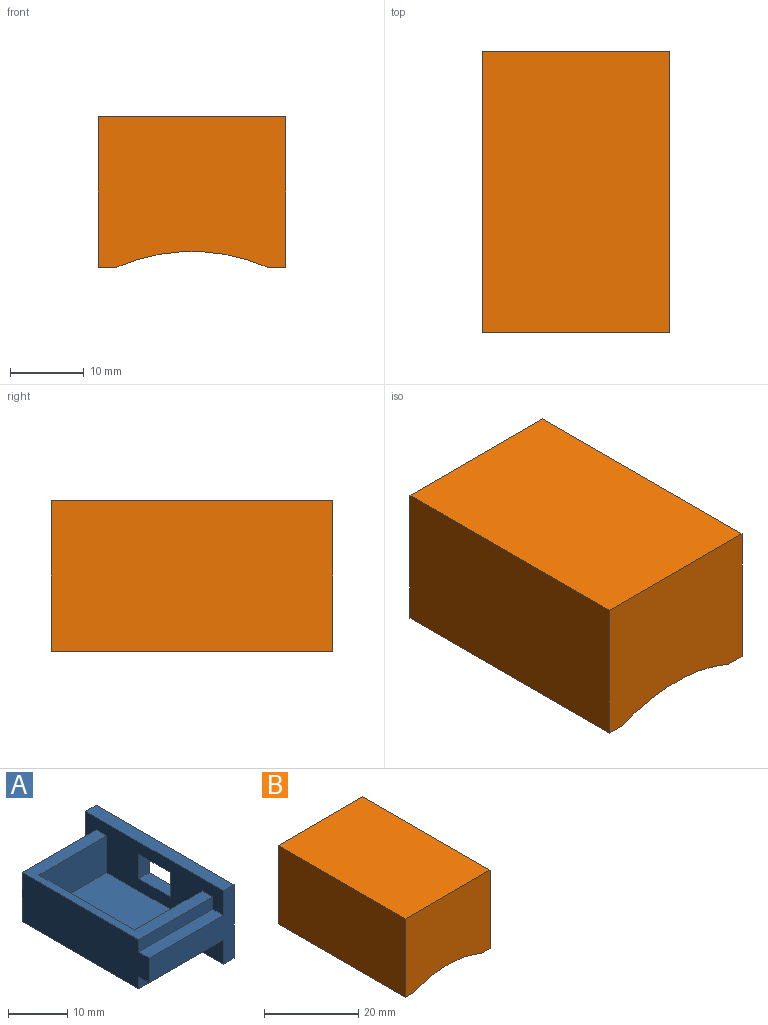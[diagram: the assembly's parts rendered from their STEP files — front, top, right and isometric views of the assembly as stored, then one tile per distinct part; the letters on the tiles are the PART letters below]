
ASSEMBLY  parts=2 mates=1
PART A: 22 faces, bbox 20.3x33x15.2 mm
  f0: plane 27.94x17.78mm, normal (0,0,1), area 125.2mm2, adj f6,f7,f12,f13,f14,f15,f16
  f1: plane 20.32x15.24mm, normal (0,-1,0), area 129mm2, adj f2,f4,f5,f6,f8,f9,f13
  f2: plane 33.02x2.54mm, normal (0,0,-1), area 83.9mm2, adj f1,f3,f5,f13
  f3: plane 15.24x2.54mm, normal (0,1,0), area 38.7mm2, adj f2,f4,f5,f13
  f4: plane 33.02x2.54mm, normal (0,0,1), area 83.9mm2, adj f1,f3,f5,f13
  f5: plane 33.02x15.24mm, normal (1,0,0), area 464.5mm2, adj f1,f2,f3,f4,f18,f19,f20,f21
  f6: plane 30.48x10.16mm, normal (-1,0,0), area 296.8mm2, adj f0,f1,f7,f8,f9,f10,f11,f12
  f7: plane 17.78x2.54mm, normal (0,-1,0), area 45.2mm2, adj f0,f6,f8,f13
  f8: plane 17.78x2.54mm, normal (0,0,1), area 45.2mm2, adj f1,f6,f7,f13
  f9: plane 17.78x2.54mm, normal (0,0,-1), area 45.2mm2, adj f1,f6,f10,f13
  f10: plane 17.78x2.54mm, normal (0,-1,0), area 45.2mm2, adj f6,f9,f11,f13
  f11: plane 27.94x17.78mm, normal (0,0,-1), area 496.8mm2, adj f6,f10,f12,f13
  f12: plane 17.78x10.16mm, normal (0,1,0), area 180.6mm2, adj f0,f6,f11,f13
  f13: plane 33.02x15.24mm, normal (-1,0,0), area 341.9mm2, adj f0,f1,f2,f3,f4,f7,f8,f9
  f14: plane 22.86x7.62mm, normal (1,0,0), area 174.2mm2, adj f0,f15,f16,f17
  f15: plane 16.26x7.62mm, normal (0,1,0), area 123.9mm2, adj f0,f13,f14,f17
  f16: plane 16.26x7.62mm, normal (0,-1,0), area 123.9mm2, adj f0,f13,f14,f17
  f17: plane 22.86x16.26mm, normal (0,0,1), area 371.6mm2, adj f13,f14,f15,f16
  f18: plane 5.08x2.54mm, normal (0,1,0), area 12.9mm2, adj f5,f13,f19,f20
  f19: plane 7.62x2.54mm, normal (0,0,1), area 19.4mm2, adj f5,f13,f18,f21
  f20: plane 7.62x2.54mm, normal (0,0,-1), area 19.4mm2, adj f5,f13,f18,f21
  f21: plane 5.08x2.54mm, normal (0,-1,0), area 12.9mm2, adj f5,f13,f19,f20
PART B: 21 faces, bbox 25.4x38.1x20.3 mm
  f0: plane 17.78x2.54mm, normal (0,1,0), area 45.2mm2, adj f1,f6,f16,f17
  f1: plane 17.78x2.54mm, normal (0,0,-1), area 45.2mm2, adj f0,f15,f16,f17
  f2: plane 17.78x2.54mm, normal (0,0,1), area 45.2mm2, adj f3,f15,f16,f17
  f3: plane 17.78x2.54mm, normal (0,1,0), area 45.2mm2, adj f2,f4,f16,f17
  f4: plane 27.94x17.78mm, normal (0,0,1), area 496.8mm2, adj f3,f5,f16,f17
  f5: plane 17.78x10.16mm, normal (0,-1,0), area 180.6mm2, adj f4,f6,f16,f17
  f6: plane 27.94x17.78mm, normal (0,0,-1), area 496.8mm2, adj f0,f5,f16,f17
  f7: plane 38.1x20.32mm, normal (1,0,0), area 271mm2, adj f8,f9,f11,f12,f15,f18,f19,f20
  f8: plane 38.1x2.54mm, normal (0,0,-1), area 96.8mm2, adj f7,f9,f11,f14
  f9: plane 25.4x20.32mm, normal (0,-1,0), area 487.2mm2, adj f7,f8,f10,f12,f13,f14
  f10: plane 38.1x20.32mm, normal (-1,0,0), area 774.2mm2, adj f9,f11,f12,f13
  f11: plane 25.4x20.32mm, normal (0,1,0), area 487.2mm2, adj f7,f8,f10,f12,f13,f14
  f12: plane 38.1x25.4mm, normal (0,0,1), area 967.7mm2, adj f7,f9,f10,f11
  f13: plane 38.1x2.54mm, normal (0,0,-1), area 96.8mm2, adj f9,f10,f11,f14
  f14: cylinder r=25.4mm len=38.1mm, axis (0,-1,0), area 796.5mm2, adj f8,f9,f11,f13
  f15: plane 20.32x15.24mm, normal (0,1,0), area 129mm2, adj f1,f2,f7,f16,f17,f18,f20
  f16: plane 30.48x10.16mm, normal (1,0,0), area 296.8mm2, adj f0,f1,f2,f3,f4,f5,f6,f15
  f17: plane 33.02x15.24mm, normal (1,0,0), area 206.5mm2, adj f0,f1,f2,f3,f4,f5,f6,f15
  f18: plane 33.02x2.54mm, normal (0,0,1), area 83.9mm2, adj f7,f15,f17,f19
  f19: plane 15.24x2.54mm, normal (0,-1,0), area 38.7mm2, adj f7,f17,f18,f20
  f20: plane 33.02x2.54mm, normal (0,0,-1), area 83.9mm2, adj f7,f15,f17,f19
PLACE A t=(22.2,10.3,-10.03)mm
PLACE B t=(17.19,7.76,-12.57)mm fixed
MATE slider B.f16 <-> A.f6  axis (1,0,0) through (22.27,26.15,-2.41)mm
